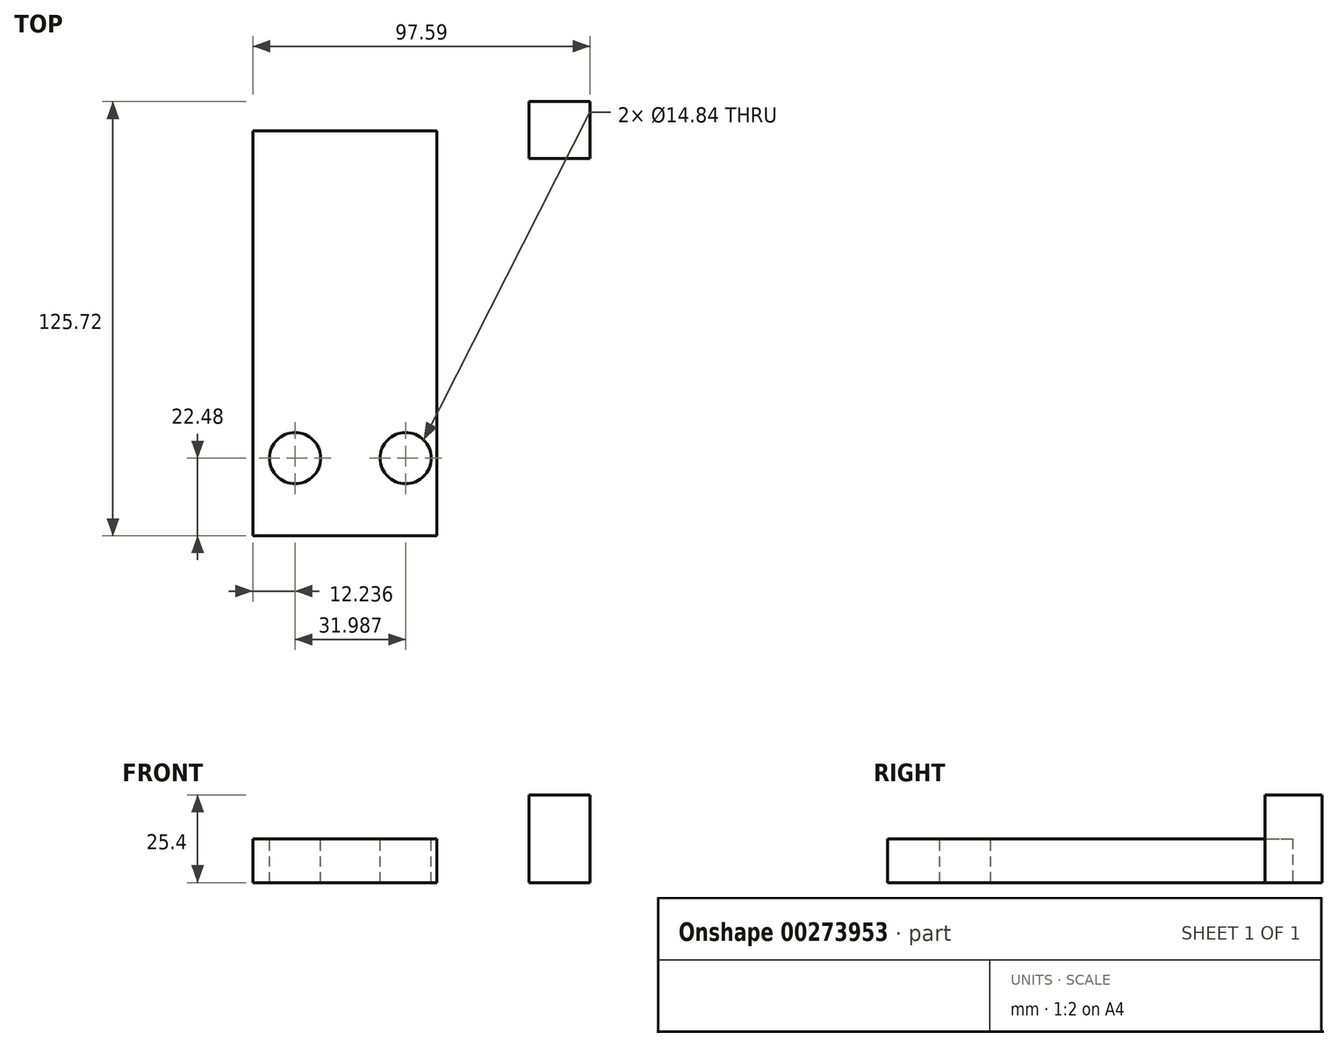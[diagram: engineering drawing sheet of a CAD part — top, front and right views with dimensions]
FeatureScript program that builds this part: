
annotation { "Feature Type Name" : "Feature", "Feature Type Description" : "" }
export const myFeature = defineFeature(function(context is Context, id is Id, definition is map)
    precondition{}
    {
        {
            var Q0;
            Q0=qCreatedBy(makeId("Top.planeOp"),FACE);
            var sketch = newSketch(context, id + "F0", { "sketchPlane" : qUnion([Q0])});
            skLineSegment(sketch, "E0.bottom", {"start": v(-28.23, -61.39) * mm, "end": v(24.95, -61.39) * mm});
            skLineSegment(sketch, "E0.top", {"start": v(-28.23, 55.8) * mm, "end": v(24.95, 55.8) * mm});
            skLineSegment(sketch, "E0.left", {"start": v(-28.23, -61.39) * mm, "end": v(-28.23, 55.8) * mm});
            skLineSegment(sketch, "E0.right", {"start": v(24.95, -61.39) * mm, "end": v(24.95, 55.8) * mm});
            skLineSegment(sketch, "E1.bottom", {"start": v(51.66, 64.33) * mm, "end": v(69.36, 64.33) * mm});
            skLineSegment(sketch, "E1.top", {"start": v(51.66, 47.85) * mm, "end": v(69.36, 47.85) * mm});
            skLineSegment(sketch, "E1.left", {"start": v(51.66, 64.33) * mm, "end": v(51.66, 47.85) * mm});
            skLineSegment(sketch, "E1.right", {"start": v(69.36, 64.33) * mm, "end": v(69.36, 47.85) * mm});
            skSolve(sketch);
        }
        {
            var Q0;
            Q0=makeQuery(id+"F0.imprint","IMPRINT",FACE,{"disambiguationData":[TD([[makeQuery(id+"F0.imprint","IMPRINT",EDGE,{"derivedFrom":sQuery(id+"F0.wireOp",EDGE,"E0.bottom")}),1.0]])]});
            extrude(context, id + "F1", {"entities" : qUnion([Q0]), "depth" : 12.7 * mm});
        }
        {
            var Q0;
            Q0=makeQuery(id+"F0.imprint","IMPRINT",FACE,{"disambiguationData":[TD([[makeQuery(id+"F0.imprint","IMPRINT",EDGE,{"derivedFrom":sQuery(id+"F0.wireOp",EDGE,"E1.bottom")}),-1.0]])]});
            extrude(context, id + "F2", {"entities" : qUnion([Q0]), "depth" : 25.4 * mm});
        }
        {
            var Q0;
            Q0=makeQuery(id+"F1.opExtrude","CAP_FACE",FACE,{"disambiguationData":[OSD([sQuery(id+"F0.wireOp",EDGE,"E0.bottom"),sQuery(id+"F0.wireOp",EDGE,"E0.top"),sQuery(id+"F0.wireOp",EDGE,"E0.left"),sQuery(id+"F0.wireOp",EDGE,"E0.right")])],"isStart":false});
            var sketch = newSketch(context, id + "F3", { "sketchPlane" : qUnion([Q0])});
            skCircle(sketch, "E2", {"center": v(-16, -38.91) * mm, "radius": 7.42 * mm});
            skLineSegment(sketch, "E3", {"start": v(0, -30.64) * mm, "end": v(0, -47.98) * mm, "construction": true});
            skCircle(sketch, "E4.MirrorC", {"center": v(16, -38.91) * mm, "radius": 7.42 * mm});
            skSolve(sketch);
        }
        {
            var Q0;
            Q0 = qSketchRegion(id + "F3", true);
            extrude(context, id + "F4", {"entities" : qUnion([Q0]), "operationType" : NewBodyOperationType.REMOVE, "oppositeDirection" : true, "depth" : 37.08 * mm});
        }
    });
